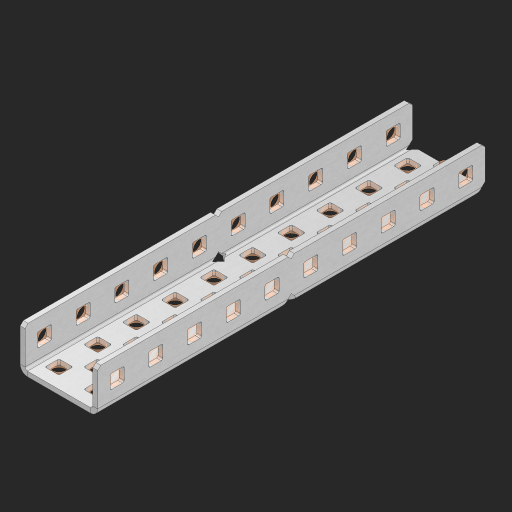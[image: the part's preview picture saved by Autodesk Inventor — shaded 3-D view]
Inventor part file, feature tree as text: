
AUTODESK INVENTOR PART (.ipt)
format: ipt  version: 2023 (Build 270158000, 158)  size: 945,152 bytes
history: native  units: in
note: dims shown in document units (in); Inventor stores cm internally (conversion verified against a paired STEP export)
features: other x57, extrude x48, sheet_metal_op x11, sketch x10, pattern_linear x2, mirror x1, chamfer x1
ambient origin geometry x8: Origin, YZ Plane, XZ Plane, XY Plane, X Axis, Y Axis, Z Axis, Center Point
bodies: Solid1 (feature_tree), Body (feature_tree)
feature tree (130):
  sheet_metal_op  "Flanges"
  other  "Flange Pattern Plane"
  other  "Flange Pattern Sketch"
  sheet_metal_op  "Flange Pattern"
  sheet_metal_op  "Body Pattern"
  pattern_linear  "Center Pattern"  Spacing1=0.0625in  [1 undecoded]
  other  "Arc Length"
  mirror  "Notch Mirror"
  pattern_linear  "Notch Pattern"  Spacing1=0.182in  [1 undecoded]
  chamfer  "End Chamfer"
  extrude  "Half Cut"  Depth=0.02in
  sketch  "Sketch1"  dims[d0=1.0in]
  other  "Plate1"
  sketch  "Sketch2"  dims[d1=5.0in]
  other  "Plate2"
  sheet_metal_op  "Bend1"
  sheet_metal_op  "Corner1"
  sketch  "Sketch3"  dims[d2=0.0625in]
  sketch  "Sketch7"  dims[d3=0.0625in]
  other  "Srf1"
  other  "Srf2"
  sketch  "Sketch8"  dims[d4=0.0312in]
  sketch  "Sketch9"  dims[d5=0.125in]
  other  "Srf91"
  sheet_metal_op  "Body Pattern Sketch"
  other  "Srf92"
  sketch  "Sketch13"  dims[d6=0.0625in]
  sketch  "Sketch14"  dims[d7=0.5in d8=90.0deg d9=0.0312in]
  sketch  "Sketch15"  dims[d10=0.25in]
  sketch  "Sketch16"  dims[d11=0.0625in d12=0.0625in d16=0.182in d17=0.02in d18=0.0625in d19=0.0in d20=0.25in d21=0.25in d38=3.937in d40=0.5in d41=0.7874in d43=1.0in d46=0.172in d47=1.0in d48=0.0in d49=0.182in d50=0.02in d51=0.25in d52=0.25in d53=0.0625in d54=0.0in d55=0.172in d56=1.0in d57=0.0in d58=0.25in d60=3.937in d62=0.5in d63=0.7874in d65=0.5in d85=0.1473in d86=0.1782in d88=0.04in d89=0.0625in d90=0.0in d91=0.04in d92=0.0491in d95=2.5in d96=0.04in d97=0.25in d98=45.0deg d99=0.25in d100=0.5in d101=0.0in d102=2.497in d106=0.182in d107=0.02in d108=0.5in d109=0.5in d110=0.0625in d111=0.0in d112=0.172in d113=0.5in d114=0.0in d117=0.5in d118=0.5in d119=0.5in]
  other  "Srf786"
  other  "Srf823"
  other  "Srf824"
  other  "Srf825"
  other  "Srf826"
  other  "Srf827"
  other  "Srf828"
  other  "Srf829"
  other  "Srf856"
  other  "Srf857"
  other  "Srf858"
  other  "Srf859"
  other  "Srf860"
  other  "Srf861"
  other  "Srf862"
  other  "Srf889"
  other  "Srf890"
  other  "Srf891"
  other  "Srf892"
  other  "Srf893"
  other  "Srf894"
  other  "Srf895"
  other  "Srf896"
  other  "Srf922"
  other  "Srf923"
  other  "Srf924"
  other  "Srf925"
  other  "Srf926"
  other  "Srf959"
  other  "Srf960"
  other  "Srf961"
  other  "Srf962"
  other  "Srf963"
  other  "Srf996"
  other  "Srf1143"
  other  "Srf1144"
  other  "Srf1145"
  other  "Srf1146"
  other  "Srf1147"
  other  "Srf1148"
  other  "Srf1199"
  other  "Srf1200"
  other  "Srf1201"
  other  "Srf1202"
  other  "Srf1203"
  other  "Srf1204"
  sheet_metal_op  "Flange Stamp"
  sheet_metal_op  "Flange Circle"
  sheet_metal_op  "Body Stamp"
  sheet_metal_op  "Body Circle"
  other  "Center Stamp"
  other  "Center Circle"
  sheet_metal_op  "Notch"
  extrude  "ExtrusionSrf2"  Depth=0.0625in
  extrude  "ExtrusionSrf92"  TaperAngle=0.0deg  [1 undecoded]
  extrude  "ExtrusionSrf823"  Depth=0.5in
  extrude  "ExtrusionSrf824"  Depth=0.5in
  extrude  "ExtrusionSrf825"  Depth=0.5in
  extrude  "ExtrusionSrf826"  Depth=0.5in
  extrude  "ExtrusionSrf827"  Depth=1.0in TaperAngle=0.0deg
  extrude  "ExtrusionSrf828"  Depth=0.5in
  extrude  "ExtrusionSrf829"  Depth=0.02in
  extrude  "ExtrusionSrf856"  Depth=0.5in
  extrude  "ExtrusionSrf857"  Depth=0.5in
  extrude  "ExtrusionSrf858"  Depth=0.0625in
  extrude  "ExtrusionSrf859"  TaperAngle=0.0deg  [1 undecoded]
  extrude  "ExtrusionSrf860"  Depth=0.5in
  extrude  "ExtrusionSrf861"  Depth=1.0in TaperAngle=0.0deg
  extrude  "ExtrusionSrf862"  Depth=0.5in
  extrude  "ExtrusionSrf889"  Depth=0.5in
  extrude  "ExtrusionSrf890"  Depth=0.5in
  extrude  "ExtrusionSrf891"  Depth=0.5in
  extrude  "ExtrusionSrf892"  Depth=0.5in
  extrude  "ExtrusionSrf893"  Depth=0.5in
  extrude  "ExtrusionSrf894"  Depth=0.0625in
  extrude  "ExtrusionSrf895"  TaperAngle=0.0deg  [1 undecoded]
  extrude  "ExtrusionSrf896"  Depth=0.5in
  extrude  "ExtrusionSrf922"  Depth=0.5in
  extrude  "ExtrusionSrf923"  Depth=2.5in
  extrude  "ExtrusionSrf924"  Depth=0.5in TaperAngle=45.0deg
  extrude  "ExtrusionSrf925"  Depth=0.5in
  extrude  "ExtrusionSrf926"  Depth=0.5in TaperAngle=0.0deg
  extrude  "ExtrusionSrf959"  Depth=0.5in
  extrude  "ExtrusionSrf960"  Depth=0.5in
  extrude  "ExtrusionSrf961"  Depth=0.02in
  extrude  "ExtrusionSrf962"  Depth=0.5in
  extrude  "ExtrusionSrf963"  Depth=0.5in
  extrude  "ExtrusionSrf996"  Depth=0.0625in
  extrude  "ExtrusionSrf1143"  TaperAngle=0.0deg  [1 undecoded]
  extrude  "ExtrusionSrf1144"  Depth=0.5in
  extrude  "ExtrusionSrf1145"  Depth=0.5in TaperAngle=0.0deg
  extrude  "ExtrusionSrf1146"  Depth=0.5in
  extrude  "ExtrusionSrf1147"  Depth=0.5in
  extrude  "ExtrusionSrf1148"  Depth=0.5in
  extrude  "ExtrusionSrf1199"  [1 undecoded]
  extrude  "ExtrusionSrf1200"  [1 undecoded]
  extrude  "ExtrusionSrf1201"  [1 undecoded]
  extrude  "ExtrusionSrf1202"  [1 undecoded]
  extrude  "ExtrusionSrf1203"  [1 undecoded]
  extrude  "ExtrusionSrf1204"  [1 undecoded]
note: 12 required parameter values undecoded (feature->parameter linkage not recoverable at this tier; creation-order binding heuristic only, values carry confidence <= 0.55)
